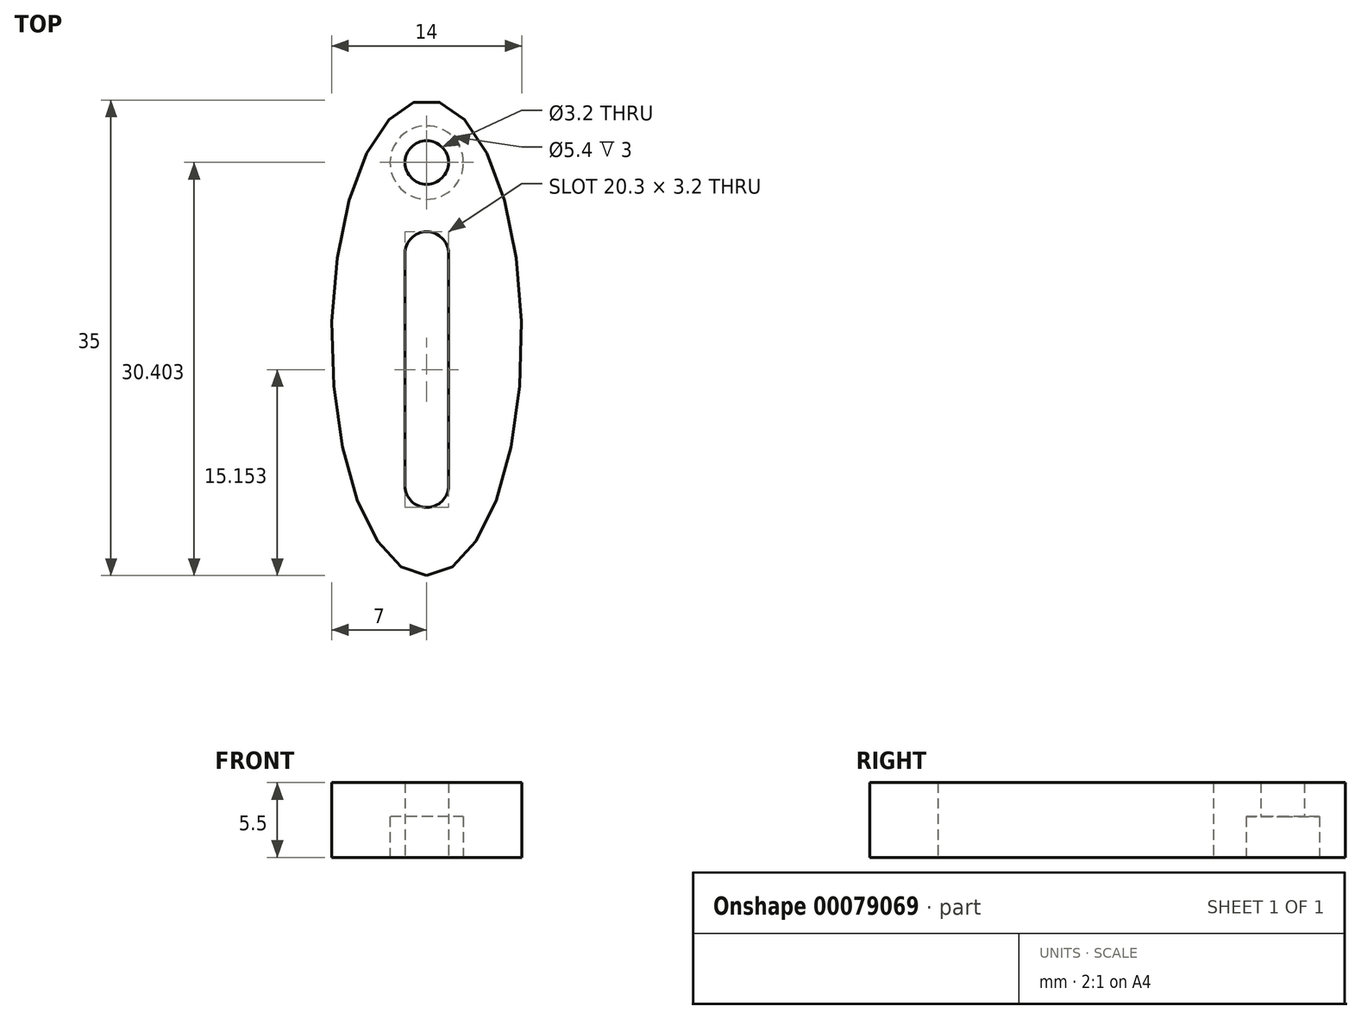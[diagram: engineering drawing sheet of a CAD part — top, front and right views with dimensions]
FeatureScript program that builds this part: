
annotation { "Feature Type Name" : "Feature", "Feature Type Description" : "" }
export const myFeature = defineFeature(function(context is Context, id is Id, definition is map)
    precondition{}
    {
        {
            var Q0;
            Q0=qCreatedBy(makeId("Top.planeOp"),FACE);
            var sketch = newSketch(context, id + "F0", { "sketchPlane" : qUnion([Q0])});
            skEllipse(sketch, "E0", {"center": v(0, 0.48) * mm, "majorRadius": 17.5 * mm, "minorRadius": 7 * mm, "majorAxis": v(0, -1)});
            skArc(sketch, "E1", {"start": v(1.6, 6.68) * mm, "mid": v(0, 8.28) * mm, "end": v(-1.6, 6.68) * mm});
            skPoint(sketch, "E2", {"position": v(0, -17.02) * mm});
            skPoint(sketch, "E3", {"position": v(0, 17.98) * mm});
            skArc(sketch, "E4", {"start": v(-1.6, -10.42) * mm, "mid": v(0, -12.02) * mm, "end": v(1.6, -10.42) * mm});
            skCircle(sketch, "E5", {"center": v(0, 13.38) * mm, "radius": 1.6 * mm});
            skLineSegment(sketch, "E6", {"start": v(-1.6, 6.68) * mm, "end": v(-1.6, -10.42) * mm});
            skLineSegment(sketch, "E7", {"start": v(1.6, 6.68) * mm, "end": v(1.6, -10.42) * mm});
            skPoint(sketch, "E7.startSnap0", {"position": v(7, 0.48) * mm});
            skSolve(sketch);
        }
        {
            var Q0;
            Q0=makeQuery(id+"F0.imprint","IMPRINT",FACE,{"disambiguationData":[TD([[makeQuery(id+"F0.imprint","IMPRINT",EDGE,{"derivedFrom":sQuery(id+"F0.wireOp",EDGE,"E0")}),1.0]])]});
            extrude(context, id + "F1", {"entities" : qUnion([Q0]), "depth" : 5.5 * mm});
        }
        {
            var Q0;
            Q0=makeQuery(id+"F1.opExtrude","CAP_FACE",FACE,{"disambiguationData":[OSD([sQuery(id+"F0.wireOp",EDGE,"E0"),sQuery(id+"F0.wireOp",EDGE,"E1"),sQuery(id+"F0.wireOp",EDGE,"E4"),sQuery(id+"F0.wireOp",EDGE,"E5"),sQuery(id+"F0.wireOp",EDGE,"E6"),sQuery(id+"F0.wireOp",EDGE,"E7")])],"isStart":false});
            var sketch = newSketch(context, id + "F2", { "sketchPlane" : qUnion([Q0])});
            skLineSegment(sketch, "E8", {"start": v(-4.96, 6.68) * mm, "end": v(-2.7, 6.68) * mm, "construction": true});
            skLineSegment(sketch, "E9", {"start": v(-4.55, -10.42) * mm, "end": v(4.43, -10.42) * mm, "construction": true});
            skArc(sketch, "E10", {"start": v(2.7, 6.68) * mm, "mid": v(0, 9.38) * mm, "end": v(-2.7, 6.68) * mm});
            skLineSegment(sketch, "E11.trimOffspring", {"start": v(2.7, 6.68) * mm, "end": v(4.82, 6.68) * mm, "construction": true});
            skArc(sketch, "E12", {"start": v(-2.7, -10.42) * mm, "mid": v(0, -13.12) * mm, "end": v(2.7, -10.42) * mm});
            skLineSegment(sketch, "E13", {"start": v(-2.7, 6.68) * mm, "end": v(-2.7, -10.42) * mm});
            skLineSegment(sketch, "E14", {"start": v(2.7, 6.68) * mm, "end": v(2.7, -10.42) * mm});
            skSolve(sketch);
        }
        {
            var Q0;
            Q0=makeQuery(id+"F0.imprint","IMPRINT",FACE,{"disambiguationData":[TD([[makeQuery(id+"F0.imprint","IMPRINT",EDGE,{"derivedFrom":sQuery(id+"F0.wireOp",EDGE,"E0")}),1.0]])]});
            var sketch = newSketch(context, id + "F3", { "sketchPlane" : qUnion([Q0])});
            skCircle(sketch, "E15", {"center": v(0, 13.38) * mm, "radius": 2.7 * mm});
            skSolve(sketch);
        }
        {
            var Q0;
            Q0=makeQuery(id+"F3.imprint","IMPRINT",FACE,{"disambiguationData":[TD([[makeQuery(id+"F3.imprint","IMPRINT",EDGE,{"derivedFrom":sQuery(id+"F3.wireOp",EDGE,"E15")}),1.0]])]});
            extrude(context, id + "F4", {"entities" : qUnion([Q0]), "operationType" : NewBodyOperationType.REMOVE, "depth" : 3 * mm});
        }
    });
